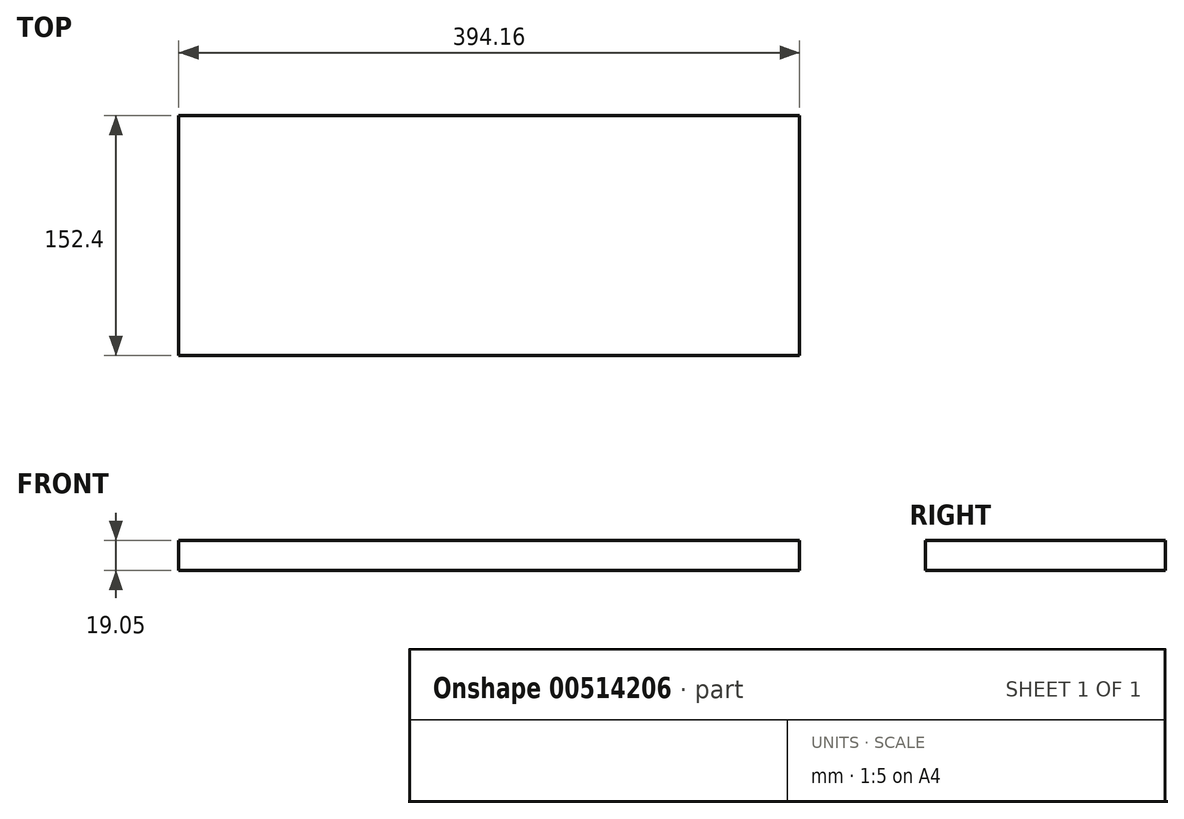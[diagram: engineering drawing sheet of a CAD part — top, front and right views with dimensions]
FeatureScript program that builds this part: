
annotation { "Feature Type Name" : "Feature", "Feature Type Description" : "" }
export const myFeature = defineFeature(function(context is Context, id is Id, definition is map)
    precondition{}
    {
        {
            var Q0;
            Q0=qCreatedBy(makeId("Top.planeOp"),FACE);
            var sketch = newSketch(context, id + "F0", { "sketchPlane" : qUnion([Q0])});
            skLineSegment(sketch, "E0.bottom", {"start": v(197.08, -76.2) * mm, "end": v(-197.08, -76.2) * mm});
            skLineSegment(sketch, "E0.top", {"start": v(197.08, 76.2) * mm, "end": v(-197.08, 76.2) * mm});
            skLineSegment(sketch, "E0.left", {"start": v(197.08, -76.2) * mm, "end": v(197.08, 76.2) * mm});
            skLineSegment(sketch, "E0.right", {"start": v(-197.08, -76.2) * mm, "end": v(-197.08, 76.2) * mm});
            skPoint(sketch, "E0.middle", {"position": v(0, 0) * mm});
            skSolve(sketch);
        }
        {
            var Q0;
            Q0=makeQuery(id+"F0.imprint","IMPRINT",FACE,{"disambiguationData":[TD([[makeQuery(id+"F0.imprint","IMPRINT",EDGE,{"derivedFrom":sQuery(id+"F0.wireOp",EDGE,"E0.bottom")}),-1.0]])]});
            extrude(context, id + "F1", {"entities" : qUnion([Q0]), "depth" : 19.05 * mm, "offsetDistance" : 25.4 * mm});
        }
    });
